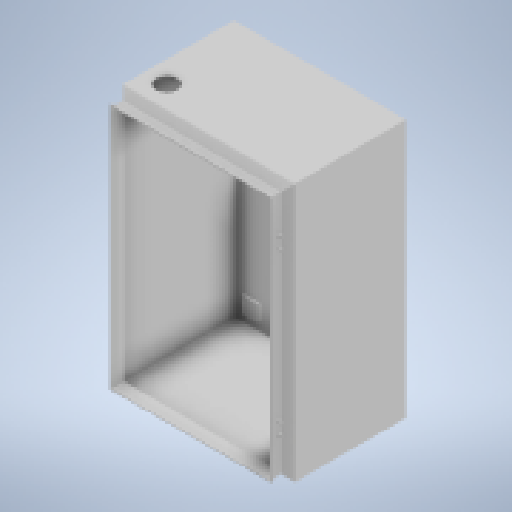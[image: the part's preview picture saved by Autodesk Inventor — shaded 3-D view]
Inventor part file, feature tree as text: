
AUTODESK INVENTOR PART (.ipt)
format: ipt  version: 2025.2 (Build 292293000, 293)  size: 948,224 bytes
history: native  units: mm
features: other x56, sketch x45, extrude x21, revolve x20, hole x4
ambient origin geometry x8: Origin, YZ Plane, XZ Plane, XY Plane, X Axis, Y Axis, Z Axis, Center Point
bodies: Solid1 (feature_tree)
feature tree (146):
  extrude  "Extrusion1"  Depth=300.0mm TaperAngle=0.0deg
  extrude  "Extrusion2"  Depth=300.0mm TaperAngle=0.0deg
  extrude  "Extrusion3"  Depth=3.25mm TaperAngle=0.0deg
  extrude  "Extrusion4"  Depth=3.25mm TaperAngle=0.0deg
  extrude  "Extrusion5"  Depth=15.297mm TaperAngle=0.0deg
  extrude  "Extrusion6"  Depth=15.297mm TaperAngle=0.0deg
  extrude  "Extrusion7"  Depth=15.297mm TaperAngle=0.0deg
  extrude  "Extrusion8"  Depth=15.297mm TaperAngle=0.0deg
  extrude  "Extrusion9"  TaperAngle=90.0deg  [1 undecoded]
  extrude  "Extrusion10"  TaperAngle=90.0deg  [1 undecoded]
  extrude  "Extrusion11"  TaperAngle=90.0deg  [1 undecoded]
  extrude  "Extrusion12"  TaperAngle=90.0deg  [1 undecoded]
  extrude  "Extrusion13"  TaperAngle=90.0deg  [1 undecoded]
  extrude  "Extrusion14"  TaperAngle=90.0deg  [1 undecoded]
  extrude  "Extrusion15"  TaperAngle=90.0deg  [1 undecoded]
  extrude  "Extrusion16"  TaperAngle=90.0deg  [1 undecoded]
  revolve  "Revolution1"  Angle=360.0deg
  revolve  "Revolution2"  Angle=360.0deg
  revolve  "Revolution3"  [1 undecoded]
  revolve  "Revolution4"  [1 undecoded]
  revolve  "Revolution5"  [1 undecoded]
  revolve  "Revolution6"  [1 undecoded]
  revolve  "Revolution7"  [1 undecoded]
  revolve  "Revolution8"  [1 undecoded]
  revolve  "Revolution9"  [1 undecoded]
  revolve  "Revolution10"  [1 undecoded]
  revolve  "Revolution11"  [1 undecoded]
  revolve  "Revolution12"  [1 undecoded]
  revolve  "Revolution13"  [1 undecoded]
  revolve  "Revolution14"  [1 undecoded]
  revolve  "Revolution15"  [1 undecoded]
  revolve  "Revolution16"  [1 undecoded]
  hole  "Hole1"  [1 undecoded]
  hole  "Hole2"  [1 undecoded]
  hole  "Hole3"  [1 undecoded]
  hole  "Hole4"  [1 undecoded]
  revolve  "Revolution17"  [1 undecoded]
  revolve  "Revolution18"  [1 undecoded]
  revolve  "Revolution19"  [1 undecoded]
  revolve  "Revolution20"  [1 undecoded]
  extrude  "Extrusion17"  [1 undecoded]
  extrude  "Extrusion18"  [1 undecoded]
  extrude  "Extrusion19"  [1 undecoded]
  extrude  "Extrusion20"  [1 undecoded]
  other  "GEHAEUSE_XY"
  other  "GEHAEUSE_YZ"
  other  "GEHAEUSE_ZX"
  other  "GEHAEUSE_X"
  other  "GEHAEUSE_Y"
  other  "GEHAEUSE_Z"
  other  "GEHAEUSE_Center"
  other  "to_HINGE_1_XY"
  other  "to_HINGE_1_YZ"
  other  "to_HINGE_1_ZX"
  other  "to_HINGE_1_X"
  other  "to_HINGE_1_Y"
  other  "to_HINGE_1_Z"
  other  "to_HINGE_1_Center"
  other  "to_HINGE_2_XY"
  other  "to_HINGE_2_YZ"
  other  "to_HINGE_2_ZX"
  other  "to_HINGE_2_X"
  other  "to_HINGE_2_Y"
  other  "to_HINGE_2_Z"
  other  "to_HINGE_2_Center"
  other  "to_L_Winkel_XY"
  other  "to_L_Winkel_YZ"
  other  "to_L_Winkel_ZX"
  other  "to_L_Winkel_X"
  other  "to_L_Winkel_Y"
  other  "to_L_Winkel_Z"
  other  "to_L_Winkel_Center"
  other  "to_L_Winkel_Bottom_XY"
  other  "to_L_Winkel_Bottom_YZ"
  other  "to_L_Winkel_Bottom_ZX"
  other  "to_L_Winkel_Bottom_X"
  other  "to_L_Winkel_Bottom_Y"
  other  "to_L_Winkel_Bottom_Z"
  other  "to_L_Winkel_Bottom_Center"
  other  "to_L_Winkel_Top_XY"
  other  "to_L_Winkel_Top_YZ"
  other  "to_L_Winkel_Top_ZX"
  other  "to_L_Winkel_Top_X"
  other  "to_L_Winkel_Top_Y"
  other  "to_L_Winkel_Top_Z"
  other  "to_L_Winkel_Top_Center"
  other  "to_L_Winkel_1_XY"
  other  "to_L_Winkel_1_YZ"
  other  "to_L_Winkel_1_ZX"
  other  "to_L_Winkel_1_X"
  other  "to_L_Winkel_1_Y"
  other  "to_L_Winkel_1_Z"
  other  "to_L_Winkel_1_Center"
  other  "to_MP_XY"
  other  "to_MP_YZ"
  other  "to_MP_ZX"
  other  "to_MP_X"
  other  "to_MP_Y"
  other  "to_MP_Z"
  other  "to_MP_Center"
  extrude  "Extrusion21"  [1 undecoded]
  sketch  "Skizze_2"  dims[d4=200.0mm d5=0.0mm d6=300.0mm d7=0.0mm]
  sketch  "Sketch_1"  dims[d0=200.0mm d1=0.0mm d2=300.0mm d3=0.0mm]
  sketch  "Sketch_37"  dims[d44=90.0deg d45=90.0deg]
  sketch  "Sketch_38"  dims[d46=90.0deg d47=90.0deg]
  sketch  "Sketch_2"  dims[d8=3.25mm d9=0.0mm d10=3.25mm d11=0.0mm]
  sketch  "Sketch_9"  dims[d12=3.25mm d13=0.0mm d14=3.25mm d15=0.0mm]
  sketch  "Sketch_10"  dims[d16=15.297mm d17=0.0mm d18=15.297mm d19=0.0mm]
  sketch  "Sketch_11"  dims[d20=15.297mm d21=0.0mm d22=15.297mm d23=0.0mm]
  sketch  "Sketch_30"  dims[d24=15.297mm d25=0.0mm d26=15.297mm d27=0.0mm]
  sketch  "Sketch_31"  dims[d28=15.297mm d29=0.0mm d30=15.297mm d31=0.0mm]
  sketch  "Sketch_32"  dims[d32=90.0deg d33=90.0deg]
  sketch  "Sketch_33"  dims[d34=90.0deg d35=90.0deg]
  sketch  "Sketch_43"  dims[d48=3.2mm d49=6.0mm d50=4.0mm d51=2.0mm d52=90.0deg d53=1.25mm d54=0.0mm]
  sketch  "Sketch_44"  dims[d55=3.2mm d56=6.0mm d57=4.0mm d58=2.0mm d59=90.0deg d60=1.25mm d61=0.0mm]
  sketch  "Sketch_45"  dims[d62=3.2mm d63=6.0mm d64=4.0mm d65=2.0mm d66=90.0deg d67=1.25mm d68=0.0mm]
  sketch  "Sketch_46"  dims[d77=360.0deg d78=360.0deg]
  sketch  "Sketch_47"  dims[d79=360.0deg d80=1.2mm d81=0.0mm]
  sketch  "Sketch_48"  dims[d82=1.2mm d83=0.0mm d84=1.2mm d85=0.0mm]
  sketch  "Sketch_49"  dims[d86=1.2mm d87=0.0mm d88=0.0mm]
  sketch  "Sketch_50"  dims[d89=0.0mm d90=0.0mm]
  sketch  "Sketch_51"  dims[d91=0.0mm d92=25.0mm]
  sketch  "Sketch_52"  dims[d93=75.0mm d94=25.0mm]
  sketch  "Sketch_53"  dims[d95=10.0mm d96=0.0mm]
  sketch  "Sketch_54"
  sketch  "Sketch_55"
  sketch  "Sketch_56"
  sketch  "Sketch_57"
  sketch  "Sketch_58"
  sketch  "Sketch_59"
  sketch  "Sketch_60"
  sketch  "Sketch_61"
  sketch  "Sketch_62"
  sketch  "Sketch33"  dims[d36=90.0deg d37=90.0deg]
  sketch  "Sketch34"  dims[d38=90.0deg d39=90.0deg]
  sketch  "Sketch35"  dims[d40=90.0deg d41=90.0deg]
  sketch  "Sketch36"  dims[d42=90.0deg d43=90.0deg]
  sketch  "Sketch_75"
  sketch  "Sketch_76"
  sketch  "Sketch_77"
  sketch  "Sketch_78"
  sketch  "Sketch_79"
  sketch  "Sketch_80"
  sketch  "Sketch_81"
  sketch  "Sketch_82"
  sketch  "Sketch45"  dims[d69=3.2mm d70=6.0mm d71=4.0mm d72=2.0mm d73=90.0deg d74=1.25mm d75=0.0mm d76=360.0deg]
note: 35 required parameter values undecoded (feature->parameter linkage not recoverable at this tier; creation-order binding heuristic only, values carry confidence <= 0.55)